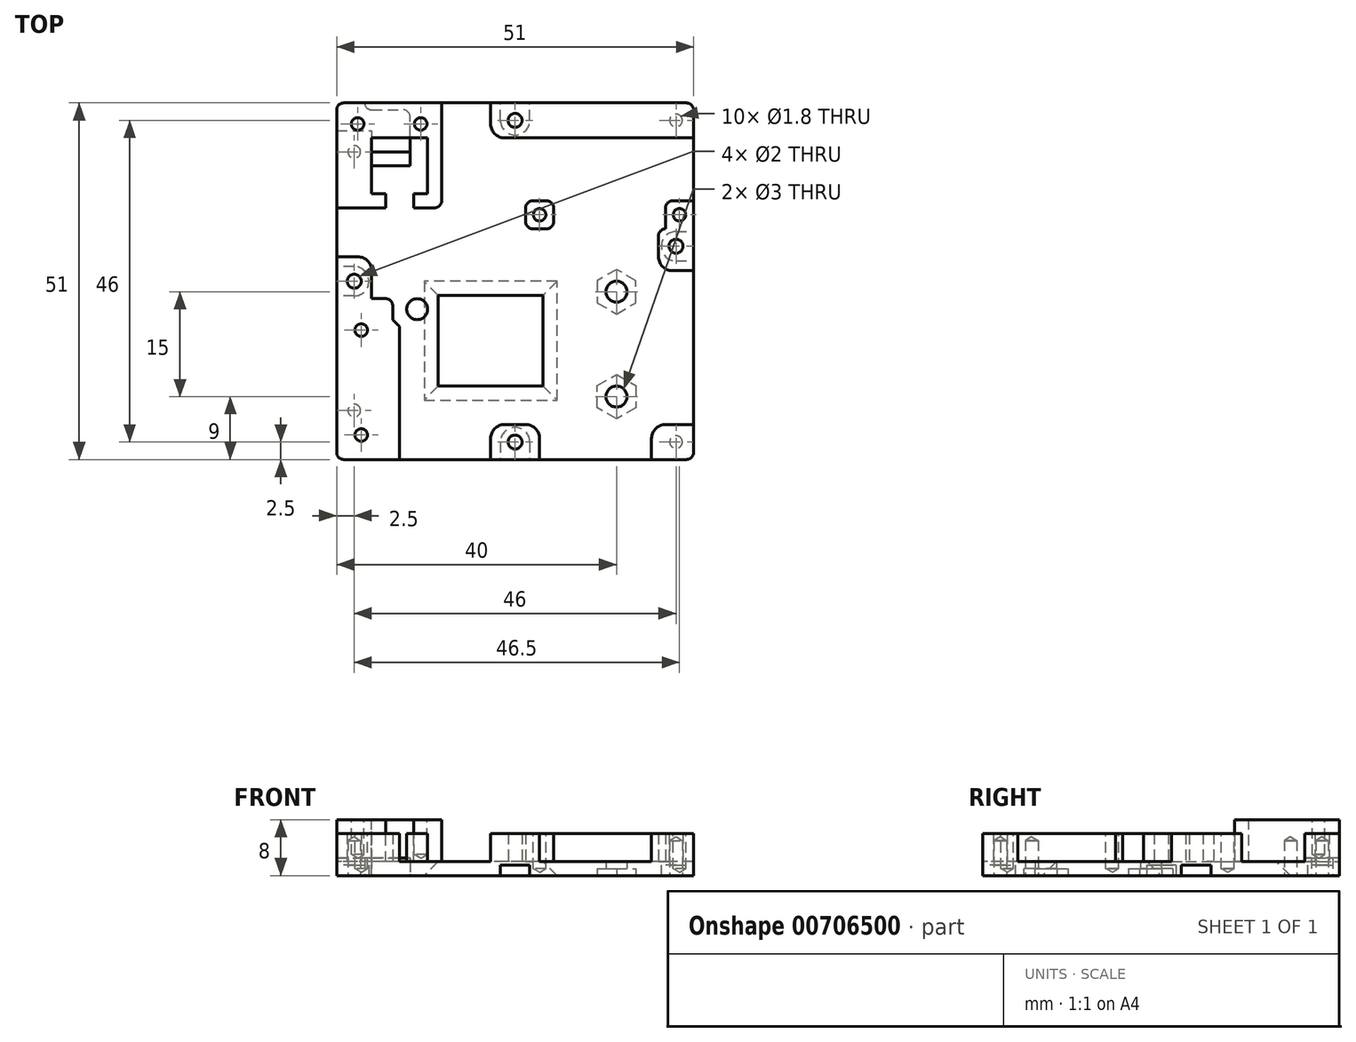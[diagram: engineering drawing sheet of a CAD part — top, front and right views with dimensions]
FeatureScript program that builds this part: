
annotation { "Feature Type Name" : "Feature", "Feature Type Description" : "" }
export const myFeature = defineFeature(function(context is Context, id is Id, definition is map)
    precondition{}
    {
        {
            var Q0;
            Q0=qCreatedBy(makeId("Top.planeOp"),FACE);
            var sketch = newSketch(context, id + "F0", { "sketchPlane" : qUnion([Q0])});
            skLineSegment(sketch, "E0.bottom", {"start": v(24.5, -25.5) * mm, "end": v(-24.5, -25.5) * mm});
            skLineSegment(sketch, "E0.top", {"start": v(24.5, 25.5) * mm, "end": v(-24.5, 25.5) * mm});
            skLineSegment(sketch, "E0.left", {"start": v(25.5, -24.5) * mm, "end": v(25.5, 24.5) * mm});
            skLineSegment(sketch, "E0.right", {"start": v(-25.5, -24.5) * mm, "end": v(-25.5, 24.5) * mm});
            skPoint(sketch, "E0.middle", {"position": v(0, 0) * mm});
            skPoint(sketch, "E1.visualSharp", {"position": v(-25.5, 25.5) * mm});
            skArc(sketch, "E1.filletArc", {"start": v(-24.5, 25.5) * mm, "mid": v(-25.2, 25.2) * mm, "end": v(-25.5, 24.5) * mm});
            skPoint(sketch, "E2.visualSharp", {"position": v(25.5, 25.5) * mm});
            skArc(sketch, "E2.filletArc", {"start": v(25.5, 24.5) * mm, "mid": v(25.2, 25.2) * mm, "end": v(24.5, 25.5) * mm});
            skPoint(sketch, "E3.visualSharp", {"position": v(25.5, -25.5) * mm});
            skArc(sketch, "E3.filletArc", {"start": v(24.5, -25.5) * mm, "mid": v(25.2, -25.2) * mm, "end": v(25.5, -24.5) * mm});
            skPoint(sketch, "E4.visualSharp", {"position": v(-25.5, -25.5) * mm});
            skArc(sketch, "E4.filletArc", {"start": v(-25.5, -24.5) * mm, "mid": v(-25.2, -25.2) * mm, "end": v(-24.5, -25.5) * mm});
            skSolve(sketch);
        }
        {
            var Q0;
            Q0=makeQuery(id+"F0.imprint","IMPRINT",FACE,{"disambiguationData":[TD([[makeQuery(id+"F0.imprint","IMPRINT",EDGE,{"derivedFrom":sQuery(id+"F0.wireOp",EDGE,"E0.bottom")}),-1.0]])]});
            extrude(context, id + "F1", {"entities" : qUnion([Q0]), "depth" : 2 * mm, "offsetDistance" : 25 * mm});
        }
        {
            var Q0;
            Q0=makeQuery(id+"F1.opExtrude","CAP_FACE",FACE,{"disambiguationData":[OSD([sQuery(id+"F0.wireOp",EDGE,"E0.bottom"),sQuery(id+"F0.wireOp",EDGE,"E0.top"),sQuery(id+"F0.wireOp",EDGE,"E0.left"),sQuery(id+"F0.wireOp",EDGE,"E0.right"),sQuery(id+"F0.wireOp",EDGE,"E1.filletArc"),sQuery(id+"F0.wireOp",EDGE,"E2.filletArc"),sQuery(id+"F0.wireOp",EDGE,"E3.filletArc"),sQuery(id+"F0.wireOp",EDGE,"E4.filletArc")])],"isStart":false});
            var sketch = newSketch(context, id + "F2", { "sketchPlane" : qUnion([Q0])});
            skLineSegment(sketch, "E5.bottom", {"start": v(-20.5, -2.5) * mm, "end": v(-25.5, -2.5) * mm});
            skLineSegment(sketch, "E5.top", {"start": v(-20.5, 2.5) * mm, "end": v(-25.5, 2.5) * mm});
            skLineSegment(sketch, "E5.left", {"start": v(-20.5, -2.5) * mm, "end": v(-20.5, 2.5) * mm});
            skLineSegment(sketch, "E5.right", {"start": v(-25.5, -2.5) * mm, "end": v(-25.5, 2.5) * mm});
            skPoint(sketch, "E5.middle", {"position": v(-23, 0) * mm});
            skLineSegment(sketch, "E6.bottom", {"start": v(2.5, 20.5) * mm, "end": v(-2.5, 20.5) * mm});
            skLineSegment(sketch, "E6.top", {"start": v(2.5, 25.5) * mm, "end": v(-2.5, 25.5) * mm});
            skLineSegment(sketch, "E6.left", {"start": v(2.5, 20.5) * mm, "end": v(2.5, 25.5) * mm});
            skLineSegment(sketch, "E6.right", {"start": v(-2.5, 20.5) * mm, "end": v(-2.5, 25.5) * mm});
            skPoint(sketch, "E6.middle", {"position": v(0, 23) * mm});
            skLineSegment(sketch, "E7.MirrorCS", {"start": v(-2.5, -20.5) * mm, "end": v(-2.5, -25.5) * mm});
            skLineSegment(sketch, "E8.MirrorCS", {"start": v(2.5, -20.5) * mm, "end": v(-2.5, -20.5) * mm});
            skLineSegment(sketch, "E9.MirrorCS", {"start": v(2.5, -25.5) * mm, "end": v(-2.5, -25.5) * mm});
            skLineSegment(sketch, "E10.MirrorCS", {"start": v(2.5, -20.5) * mm, "end": v(2.5, -25.5) * mm});
            skPoint(sketch, "E11.MirrorP", {"position": v(0, -23) * mm});
            skLineSegment(sketch, "E12.bottom", {"start": v(25.5, 2.5) * mm, "end": v(20.5, 2.5) * mm});
            skLineSegment(sketch, "E12.top", {"start": v(25.5, 7.5) * mm, "end": v(20.5, 7.5) * mm});
            skLineSegment(sketch, "E12.left", {"start": v(25.5, 2.5) * mm, "end": v(25.5, 7.5) * mm});
            skLineSegment(sketch, "E12.right", {"start": v(20.5, 2.5) * mm, "end": v(20.5, 7.5) * mm});
            skPoint(sketch, "E12.middle", {"position": v(23, 5) * mm});
            skLineSegment(sketch, "E13.bottom", {"start": v(-10.5, 10.5) * mm, "end": v(-25.5, 10.5) * mm});
            skLineSegment(sketch, "E13.top", {"start": v(-10.5, 25.5) * mm, "end": v(-24.5, 25.5) * mm});
            skLineSegment(sketch, "E13.left", {"start": v(-10.5, 10.5) * mm, "end": v(-10.5, 25.5) * mm});
            skLineSegment(sketch, "E13.right", {"start": v(-25.5, 10.5) * mm, "end": v(-25.5, 24.5) * mm});
            skPoint(sketch, "E13.middle", {"position": v(-18, 18) * mm});
            skPoint(sketch, "E14.visualSharp", {"position": v(-25.5, 25.5) * mm});
            skArc(sketch, "E14.filletArc", {"start": v(-24.5, 25.5) * mm, "mid": v(-25.2, 25.2) * mm, "end": v(-25.5, 24.5) * mm});
            skLineSegment(sketch, "E15.bottom", {"start": v(4, -15) * mm, "end": v(-11, -15) * mm});
            skLineSegment(sketch, "E15.top", {"start": v(4, -2) * mm, "end": v(-11, -2) * mm});
            skLineSegment(sketch, "E15.left", {"start": v(4, -15) * mm, "end": v(4, -2) * mm});
            skLineSegment(sketch, "E15.right", {"start": v(-11, -15) * mm, "end": v(-11, -2) * mm});
            skPoint(sketch, "E15.middle", {"position": v(-3.5, -8.5) * mm});
            skSolve(sketch);
        }
        {
            var Q0;
            Q0=makeQuery(id+"F2.imprint","IMPRINT",FACE,{"disambiguationData":[TD([[makeQuery(id+"F2.imprint","IMPRINT",EDGE,{"derivedFrom":sQuery(id+"F2.wireOp",EDGE,"E5.bottom")}),-1.0]])]});
            var Q1;
            Q1=makeQuery(id+"F2.imprint","IMPRINT",FACE,{"disambiguationData":[TD([[makeQuery(id+"F2.imprint","IMPRINT",EDGE,{"derivedFrom":sQuery(id+"F2.wireOp",EDGE,"E6.bottom")}),-1.0]])]});
            var Q2;
            Q2=makeQuery(id+"F2.imprint","IMPRINT",FACE,{"disambiguationData":[TD([[makeQuery(id+"F2.imprint","IMPRINT",EDGE,{"derivedFrom":sQuery(id+"F2.wireOp",EDGE,"E12.bottom")}),-1.0]])]});
            var Q3;
            Q3=makeQuery(id+"F2.imprint","IMPRINT",FACE,{"disambiguationData":[TD([[makeQuery(id+"F2.imprint","IMPRINT",EDGE,{"derivedFrom":sQuery(id+"F2.wireOp",EDGE,"E7.MirrorCS")}),1.0]])]});
            extrude(context, id + "F3", {"entities" : qUnion([Q0, Q1, Q2, Q3]), "operationType" : NewBodyOperationType.ADD, "depth" : 4 * mm, "offsetDistance" : 25 * mm});
        }
        {
            var Q0;
            Q0=makeQuery(id+"F2.imprint","IMPRINT",FACE,{"disambiguationData":[TD([[makeQuery(id+"F2.imprint","IMPRINT",EDGE,{"derivedFrom":sQuery(id+"F2.wireOp",EDGE,"E13.bottom")}),-1.0]])]});
            extrude(context, id + "F4", {"entities" : qUnion([Q0]), "operationType" : NewBodyOperationType.ADD, "depth" : 6 * mm, "offsetDistance" : 25 * mm});
        }
        {
            var Q0;
            Q0=makeQuery(id+"F4.opExtrude","SWEPT_EDGE",EDGE,{"disambiguationData":[OSD([sQuery(id+"F2.wireOp",EDGE,"E13.bottom"),sQuery(id+"F2.wireOp",EDGE,"E13.left")])]});
            fillet(context, id + "F5", {"entities" : qUnion([Q0]), "radius" : 1 * mm, "tangentPropagation" : true, "allowEdgeOverflow" : false});
        }
        {
            var Q0;
            Q0=makeQuery(id+"F1.opExtrude","CAP_FACE",FACE,{"disambiguationData":[OSD([sQuery(id+"F0.wireOp",EDGE,"E0.bottom"),sQuery(id+"F0.wireOp",EDGE,"E0.top"),sQuery(id+"F0.wireOp",EDGE,"E0.left"),sQuery(id+"F0.wireOp",EDGE,"E0.right"),sQuery(id+"F0.wireOp",EDGE,"E1.filletArc"),sQuery(id+"F0.wireOp",EDGE,"E2.filletArc"),sQuery(id+"F0.wireOp",EDGE,"E3.filletArc"),sQuery(id+"F0.wireOp",EDGE,"E4.filletArc")])],"isStart":true});
            var sketch = newSketch(context, id + "F6", { "sketchPlane" : qUnion([Q0])});
            skPoint(sketch, "E16", {"position": v(0, 23) * mm});
            skPoint(sketch, "E17", {"position": v(-23, 0) * mm});
            skPoint(sketch, "E18", {"position": v(23, -5) * mm});
            skPoint(sketch, "E19.MirrorP", {"position": v(0, -23) * mm});
            skSolve(sketch);
        }
        {
            var Q0;
            Q0=sQuery(id+"F6.wireOp",VERTEX,"E17");
            var Q1;
            Q1=sQuery(id+"F6.wireOp",VERTEX,"E16");
            var Q2;
            Q2=sQuery(id+"F6.wireOp",VERTEX,"E18");
            var Q3;
            Q3=sQuery(id+"F6.wireOp",VERTEX,"E19.MirrorP");
            var Q4;
            Q4=makeQuery(id+"F1.opExtrude","SWEPT_BODY",BODY,{"disambiguationData":[OSD([sQuery(id+"F0.wireOp",EDGE,"E0.bottom"),sQuery(id+"F0.wireOp",EDGE,"E0.top"),sQuery(id+"F0.wireOp",EDGE,"E0.left"),sQuery(id+"F0.wireOp",EDGE,"E0.right"),sQuery(id+"F0.wireOp",EDGE,"E1.filletArc"),sQuery(id+"F0.wireOp",EDGE,"E2.filletArc"),sQuery(id+"F0.wireOp",EDGE,"E3.filletArc"),sQuery(id+"F0.wireOp",EDGE,"E4.filletArc")])]});
            hole(context, id + "F7", {"style" : HoleStyle.C_BORE, "endStyle" : HoleEndStyle.THROUGH, "holeDiameter" : 2 * mm, "cBoreDiameter" : 4.2 * mm, "cBoreDepth" : 1.5 * mm, "majorDiameter" : 5 * mm, "isTappedThrough" : true, "tappedDepth" : 6 * mm, "tapClearance" : 3, "locations" : qUnion([Q0, Q1, Q2, Q3]), "scope" : qUnion([Q4])});
        }
        {
            var Q0;
            Q0=makeQuery(id+"F2.imprint","IMPRINT",FACE,{"disambiguationData":[TD([[makeQuery(id+"F2.imprint","IMPRINT",EDGE,{"derivedFrom":sQuery(id+"F2.wireOp",EDGE,"E15.bottom")}),-1.0]])]});
            extrude(context, id + "F8", {"entities" : qUnion([Q0]), "operationType" : NewBodyOperationType.REMOVE, "oppositeDirection" : true, "depth" : 25 * mm, "offsetDistance" : 25 * mm});
        }
        {
            var Q0;
            Q0=makeQuery(id+"F8.boolean.opBoolean","INTERSECT",EDGE,{"derivedFrom":[makeQuery(id+"F1.opExtrude","CAP_FACE",FACE,{"disambiguationData":[OSD([sQuery(id+"F0.wireOp",EDGE,"E0.bottom"),sQuery(id+"F0.wireOp",EDGE,"E0.top"),sQuery(id+"F0.wireOp",EDGE,"E0.left"),sQuery(id+"F0.wireOp",EDGE,"E0.right"),sQuery(id+"F0.wireOp",EDGE,"E1.filletArc"),sQuery(id+"F0.wireOp",EDGE,"E2.filletArc"),sQuery(id+"F0.wireOp",EDGE,"E3.filletArc"),sQuery(id+"F0.wireOp",EDGE,"E4.filletArc")])],"isStart":true}),makeQuery(id+"F8.opExtrude","SWEPT_FACE",FACE,{"disambiguationData":[OSD([sQuery(id+"F2.wireOp",EDGE,"E15.right")])]})]});
            var Q1;
            Q1=makeQuery(id+"F8.boolean.opBoolean","INTERSECT",EDGE,{"derivedFrom":[makeQuery(id+"F1.opExtrude","CAP_FACE",FACE,{"disambiguationData":[OSD([sQuery(id+"F0.wireOp",EDGE,"E0.bottom"),sQuery(id+"F0.wireOp",EDGE,"E0.top"),sQuery(id+"F0.wireOp",EDGE,"E0.left"),sQuery(id+"F0.wireOp",EDGE,"E0.right"),sQuery(id+"F0.wireOp",EDGE,"E1.filletArc"),sQuery(id+"F0.wireOp",EDGE,"E2.filletArc"),sQuery(id+"F0.wireOp",EDGE,"E3.filletArc"),sQuery(id+"F0.wireOp",EDGE,"E4.filletArc")])],"isStart":true}),makeQuery(id+"F8.opExtrude","SWEPT_FACE",FACE,{"disambiguationData":[OSD([sQuery(id+"F2.wireOp",EDGE,"E15.bottom")])]})]});
            var Q2;
            Q2=makeQuery(id+"F8.boolean.opBoolean","INTERSECT",EDGE,{"derivedFrom":[makeQuery(id+"F1.opExtrude","CAP_FACE",FACE,{"disambiguationData":[OSD([sQuery(id+"F0.wireOp",EDGE,"E0.bottom"),sQuery(id+"F0.wireOp",EDGE,"E0.top"),sQuery(id+"F0.wireOp",EDGE,"E0.left"),sQuery(id+"F0.wireOp",EDGE,"E0.right"),sQuery(id+"F0.wireOp",EDGE,"E1.filletArc"),sQuery(id+"F0.wireOp",EDGE,"E2.filletArc"),sQuery(id+"F0.wireOp",EDGE,"E3.filletArc"),sQuery(id+"F0.wireOp",EDGE,"E4.filletArc")])],"isStart":true}),makeQuery(id+"F8.opExtrude","SWEPT_FACE",FACE,{"disambiguationData":[OSD([sQuery(id+"F2.wireOp",EDGE,"E15.left")])]})]});
            var Q3;
            Q3=makeQuery(id+"F8.boolean.opBoolean","INTERSECT",EDGE,{"derivedFrom":[makeQuery(id+"F1.opExtrude","CAP_FACE",FACE,{"disambiguationData":[OSD([sQuery(id+"F0.wireOp",EDGE,"E0.bottom"),sQuery(id+"F0.wireOp",EDGE,"E0.top"),sQuery(id+"F0.wireOp",EDGE,"E0.left"),sQuery(id+"F0.wireOp",EDGE,"E0.right"),sQuery(id+"F0.wireOp",EDGE,"E1.filletArc"),sQuery(id+"F0.wireOp",EDGE,"E2.filletArc"),sQuery(id+"F0.wireOp",EDGE,"E3.filletArc"),sQuery(id+"F0.wireOp",EDGE,"E4.filletArc")])],"isStart":true}),makeQuery(id+"F8.opExtrude","SWEPT_FACE",FACE,{"disambiguationData":[OSD([sQuery(id+"F2.wireOp",EDGE,"E15.top")])]})]});
            chamfer(context, id + "F9", {"entities" : qUnion([Q0, Q1, Q2, Q3]), "width" : 2 * mm, "tangentPropagation" : true});
        }
        {
            var Q0;
            {var subQ11=sQuery(id+"F2.wireOp",EDGE,"E5.bottom");Q0=makeQuery(id+"F2.imprint","IMPRINT",FACE,{"disambiguationData":[TD([[makeQuery(id+"F2.imprint","IMPRINT",EDGE,{"derivedFrom":subQ11}),1.0]])]});}
            var sketch = newSketch(context, id + "F10", { "sketchPlane" : qUnion([Q0])});
            skLineSegment(sketch, "E20.bottom", {"start": v(-16.5, -25.5) * mm, "end": v(-24.5, -25.5) * mm});
            skLineSegment(sketch, "E20.left", {"start": v(-12.5, -25.5) * mm, "end": v(-12.5, -4) * mm, "construction": true});
            skLineSegment(sketch, "E20.right", {"start": v(-25.5, -24.5) * mm, "end": v(-25.5, -2.5) * mm});
            skPoint(sketch, "E20.middle", {"position": v(-19, -14) * mm});
            skPoint(sketch, "E21.visualSharp", {"position": v(-25.5, -25.5) * mm});
            skArc(sketch, "E21.filletArc", {"start": v(-25.5, -24.5) * mm, "mid": v(-25.2, -25.2) * mm, "end": v(-24.5, -25.5) * mm});
            skCircle(sketch, "E22", {"center": v(-14, -4) * mm, "radius": 1.5 * mm});
            skLineSegment(sketch, "E23", {"start": v(-16.5, -6.5) * mm, "end": v(-16.5, -25.5) * mm});
            skLineSegment(sketch, "E24.trimOffspring", {"start": v(-18.5, -2.5) * mm, "end": v(-25.5, -2.5) * mm});
            skLineSegment(sketch, "E25", {"start": v(-17.5, -3.5) * mm, "end": v(-17.5, -5.5) * mm});
            skLineSegment(sketch, "E26", {"start": v(-16.5, -6.5) * mm, "end": v(-17.5, -5.5) * mm});
            skPoint(sketch, "E27.visualSharp", {"position": v(-17.5, -2.5) * mm});
            skArc(sketch, "E27.filletArc", {"start": v(-17.5, -3.5) * mm, "mid": v(-17.8, -2.8) * mm, "end": v(-18.5, -2.5) * mm});
            skSolve(sketch);
        }
        {
            var Q0;
            Q0=makeQuery(id+"F10.imprint","IMPRINT",FACE,{"disambiguationData":[TD([[makeQuery(id+"F10.imprint","IMPRINT",EDGE,{"derivedFrom":sQuery(id+"F10.wireOp",EDGE,"E20.bottom")}),-1.0]])]});
            var Q1;
            Q1=makeQuery(id+"F10.imprint","IMPRINT",FACE,{"disambiguationData":[TD([[makeQuery(id+"F10.imprint","IMPRINT",EDGE,{"derivedFrom":sQuery(id+"F10.wireOp",EDGE,"E22")}),1.0]])]});
            extrude(context, id + "F11", {"entities" : qUnion([Q0, Q1]), "operationType" : NewBodyOperationType.ADD, "depth" : 4 * mm, "offsetDistance" : 25 * mm});
        }
        {
            var Q0;
            Q0=makeQuery(id+"F11.boolean.opBoolean","MERGE",FACE,{"derivedFrom":[makeQuery(id+"F3.opExtrude","CAP_FACE",FACE,{"disambiguationData":[OSD([sQuery(id+"F2.wireOp",EDGE,"E5.bottom"),sQuery(id+"F2.wireOp",EDGE,"E5.top"),sQuery(id+"F2.wireOp",EDGE,"E5.left"),sQuery(id+"F2.wireOp",EDGE,"E5.right")])],"isStart":false}),makeQuery(id+"F11.opExtrude","CAP_FACE",FACE,{"disambiguationData":[OSD([sQuery(id+"F10.wireOp",EDGE,"E20.bottom"),sQuery(id+"F10.wireOp",EDGE,"E20.right"),sQuery(id+"F10.wireOp",EDGE,"E21.filletArc"),sQuery(id+"F10.wireOp",EDGE,"E23"),sQuery(id+"F10.wireOp",EDGE,"E24.trimOffspring"),sQuery(id+"F10.wireOp",EDGE,"E25"),sQuery(id+"F10.wireOp",EDGE,"E26"),sQuery(id+"F10.wireOp",EDGE,"E27.filletArc")])],"isStart":false})]});
            var sketch = newSketch(context, id + "F12", { "sketchPlane" : qUnion([Q0])});
            skPoint(sketch, "E28", {"position": v(-22, -22) * mm});
            skPoint(sketch, "E29", {"position": v(-22, -7) * mm});
            skSolve(sketch);
        }
        {
            var Q0;
            Q0=makeQuery(id+"F4.opExtrude","CAP_FACE",FACE,{"disambiguationData":[OSD([sQuery(id+"F2.wireOp",EDGE,"E13.bottom"),sQuery(id+"F2.wireOp",EDGE,"E13.top"),sQuery(id+"F2.wireOp",EDGE,"E13.left"),sQuery(id+"F2.wireOp",EDGE,"E13.right"),sQuery(id+"F2.wireOp",EDGE,"E14.filletArc")])],"isStart":false});
            var sketch = newSketch(context, id + "F13", { "sketchPlane" : qUnion([Q0])});
            skPoint(sketch, "E30", {"position": v(-22.5, 22.5) * mm});
            skPoint(sketch, "E31", {"position": v(-13.5, 22.5) * mm});
            skLineSegment(sketch, "E32.bottom", {"start": v(-12.5, 12.5) * mm, "end": v(-14.5, 12.5) * mm});
            skLineSegment(sketch, "E32.top", {"start": v(-12.5, 20.5) * mm, "end": v(-23.5, 20.5) * mm});
            skLineSegment(sketch, "E32.left", {"start": v(-12.5, 12.5) * mm, "end": v(-12.5, 20.5) * mm});
            skLineSegment(sketch, "E32.right", {"start": v(-23.5, 12.5) * mm, "end": v(-23.5, 20.5) * mm});
            skPoint(sketch, "E32.middle", {"position": v(-18, 16.5) * mm});
            skLineSegment(sketch, "E33", {"start": v(-14.5, 10.5) * mm, "end": v(-18.5, 10.5) * mm});
            skLineSegment(sketch, "E34", {"start": v(-18.5, 10.5) * mm, "end": v(-18.5, 12.5) * mm});
            skLineSegment(sketch, "E35", {"start": v(-14.5, 10.5) * mm, "end": v(-14.5, 12.5) * mm});
            skLineSegment(sketch, "E36.trimOffspring", {"start": v(-18.5, 12.5) * mm, "end": v(-23.5, 12.5) * mm});
            skSolve(sketch);
        }
        {
            var Q0;
            Q0=makeQuery(id+"F13.imprint","IMPRINT",FACE,{"disambiguationData":[TD([[makeQuery(id+"F13.imprint","IMPRINT",EDGE,{"derivedFrom":sQuery(id+"F13.wireOp",EDGE,"E32.bottom")}),-1.0]])]});
            extrude(context, id + "F14", {"entities" : qUnion([Q0]), "operationType" : NewBodyOperationType.REMOVE, "oppositeDirection" : true, "depth" : 6 * mm, "offsetDistance" : 25 * mm});
        }
        {
            var Q0;
            Q0=makeQuery(id+"F1.opExtrude","CAP_FACE",FACE,{"disambiguationData":[OSD([sQuery(id+"F0.wireOp",EDGE,"E0.bottom"),sQuery(id+"F0.wireOp",EDGE,"E0.top"),sQuery(id+"F0.wireOp",EDGE,"E0.left"),sQuery(id+"F0.wireOp",EDGE,"E0.right"),sQuery(id+"F0.wireOp",EDGE,"E1.filletArc"),sQuery(id+"F0.wireOp",EDGE,"E2.filletArc"),sQuery(id+"F0.wireOp",EDGE,"E3.filletArc"),sQuery(id+"F0.wireOp",EDGE,"E4.filletArc")])],"isStart":true});
            var sketch = newSketch(context, id + "F15", { "sketchPlane" : qUnion([Q0])});
            skCircle(sketch, "E37.0", {"center": v(0, 23) * mm, "radius": 2.1 * mm});
            skCircle(sketch, "E37.1", {"center": v(-23, 0) * mm, "radius": 2.1 * mm});
            skCircle(sketch, "E37.2", {"center": v(0, -23) * mm, "radius": 2.1 * mm});
            skCircle(sketch, "E37.3", {"center": v(23, -5) * mm, "radius": 2.1 * mm});
            skLineSegment(sketch, "E38", {"start": v(2.1, 23) * mm, "end": v(2.1, 25.5) * mm});
            skLineSegment(sketch, "E39.MirrorCS", {"start": v(-2.1, 23) * mm, "end": v(-2.1, 25.5) * mm});
            skLineSegment(sketch, "E40.MirrorCS", {"start": v(-2.1, -23) * mm, "end": v(-2.1, -25.5) * mm});
            skLineSegment(sketch, "E41.MirrorCS", {"start": v(2.1, -23) * mm, "end": v(2.1, -25.5) * mm});
            skLineSegment(sketch, "E42", {"start": v(-23, 2.1) * mm, "end": v(-25.5, 2.1) * mm});
            skLineSegment(sketch, "E43.MirrorCS", {"start": v(-23, -2.1) * mm, "end": v(-25.5, -2.1) * mm});
            skLineSegment(sketch, "E44", {"start": v(23, -2.9) * mm, "end": v(25.5, -2.9) * mm});
            skLineSegment(sketch, "E45", {"start": v(23, -7.1) * mm, "end": v(25.5, -7.1) * mm});
            skSolve(sketch);
        }
        {
            var Q0;
            {var subQ0=sQuery(id+"F15.wireOp",EDGE,"E38");Q0=makeQuery(id+"F15.imprint","IMPRINT",FACE,{"disambiguationData":[TD([[makeQuery(id+"F15.imprint","IMPRINT",EDGE,{"derivedFrom":subQ0}),1.0]])]});}
            var Q1;
            {var subQ0=sQuery(id+"F15.wireOp",EDGE,"E44");Q1=makeQuery(id+"F15.imprint","IMPRINT",FACE,{"disambiguationData":[TD([[makeQuery(id+"F15.imprint","IMPRINT",EDGE,{"derivedFrom":subQ0}),-1.0]])]});}
            var Q2;
            {var subQ0=sQuery(id+"F15.wireOp",EDGE,"E42");Q2=makeQuery(id+"F15.imprint","IMPRINT",FACE,{"disambiguationData":[TD([[makeQuery(id+"F15.imprint","IMPRINT",EDGE,{"derivedFrom":subQ0}),1.0]])]});}
            var Q3;
            {var subQ0=sQuery(id+"F15.wireOp",EDGE,"E40.MirrorCS");Q3=makeQuery(id+"F15.imprint","IMPRINT",FACE,{"disambiguationData":[TD([[makeQuery(id+"F15.imprint","IMPRINT",EDGE,{"derivedFrom":subQ0}),1.0]])]});}
            extrude(context, id + "F16", {"entities" : qUnion([Q0, Q1, Q2, Q3]), "operationType" : NewBodyOperationType.REMOVE, "oppositeDirection" : true, "depth" : 1.5 * mm, "offsetDistance" : 25 * mm});
        }
        {
            var Q0;
            Q0=makeQuery(id+"F1.opExtrude","CAP_FACE",FACE,{"disambiguationData":[OSD([sQuery(id+"F0.wireOp",EDGE,"E0.bottom"),sQuery(id+"F0.wireOp",EDGE,"E0.top"),sQuery(id+"F0.wireOp",EDGE,"E0.left"),sQuery(id+"F0.wireOp",EDGE,"E0.right"),sQuery(id+"F0.wireOp",EDGE,"E1.filletArc"),sQuery(id+"F0.wireOp",EDGE,"E2.filletArc"),sQuery(id+"F0.wireOp",EDGE,"E3.filletArc"),sQuery(id+"F0.wireOp",EDGE,"E4.filletArc")])],"isStart":true});
            var sketch = newSketch(context, id + "F17", { "sketchPlane" : qUnion([Q0])});
            skPoint(sketch, "E46", {"position": v(14.5, 1.5) * mm});
            skPoint(sketch, "E47", {"position": v(14.5, 16.5) * mm});
            skCircle(sketch, "E48.cCircle", {"center": v(14.5, 1.5) * mm, "radius": 2.75 * mm, "construction": true});
            skLineSegment(sketch, "E48.0", {"start": v(17.25, 3.09) * mm, "end": v(17.25, -0.09) * mm});
            skLineSegment(sketch, "E48.1", {"start": v(17.25, -0.09) * mm, "end": v(14.5, -1.68) * mm});
            skLineSegment(sketch, "E48.2", {"start": v(14.5, -1.68) * mm, "end": v(11.75, -0.09) * mm});
            skLineSegment(sketch, "E48.3", {"start": v(11.75, -0.09) * mm, "end": v(11.75, 3.09) * mm});
            skLineSegment(sketch, "E48.4", {"start": v(11.75, 3.09) * mm, "end": v(14.5, 4.68) * mm});
            skLineSegment(sketch, "E48.5", {"start": v(14.5, 4.68) * mm, "end": v(17.25, 3.09) * mm});
            skPoint(sketch, "E48.0.midPoint", {"position": v(17.25, 1.5) * mm});
            skLineSegment(sketch, "E49", {"start": v(42.06, 9) * mm, "end": v(-2.43, 9) * mm, "construction": true});
            skCircle(sketch, "E50.MirrorC", {"center": v(14.5, 16.5) * mm, "radius": 2.75 * mm, "construction": true});
            skLineSegment(sketch, "E51.MirrorCS", {"start": v(14.5, 19.68) * mm, "end": v(11.75, 18.09) * mm});
            skLineSegment(sketch, "E52.MirrorCS", {"start": v(17.25, 18.09) * mm, "end": v(14.5, 19.68) * mm});
            skLineSegment(sketch, "E53.MirrorCS", {"start": v(17.25, 14.91) * mm, "end": v(17.25, 18.09) * mm});
            skLineSegment(sketch, "E54.MirrorCS", {"start": v(14.5, 13.32) * mm, "end": v(17.25, 14.91) * mm});
            skLineSegment(sketch, "E55.MirrorCS", {"start": v(11.75, 14.91) * mm, "end": v(14.5, 13.32) * mm});
            skLineSegment(sketch, "E56.MirrorCS", {"start": v(11.75, 18.09) * mm, "end": v(11.75, 14.91) * mm});
            skSolve(sketch);
        }
        {
            var Q0;
            Q0=makeQuery(id+"F17.imprint","IMPRINT",FACE,{"disambiguationData":[TD([[makeQuery(id+"F17.imprint","IMPRINT",EDGE,{"derivedFrom":sQuery(id+"F17.wireOp",EDGE,"E51.MirrorCS")}),1.0]])]});
            var Q1;
            Q1=makeQuery(id+"F17.imprint","IMPRINT",FACE,{"disambiguationData":[TD([[makeQuery(id+"F17.imprint","IMPRINT",EDGE,{"derivedFrom":sQuery(id+"F17.wireOp",EDGE,"E48.0")}),-1.0]])]});
            extrude(context, id + "F18", {"entities" : qUnion([Q0, Q1]), "operationType" : NewBodyOperationType.REMOVE, "oppositeDirection" : true, "depth" : 1 * mm, "offsetDistance" : 25 * mm});
        }
        {
            var Q0;
            Q0=sQuery(id+"F17.wireOp",VERTEX,"E50.MirrorC.center");
            var Q1;
            Q1=sQuery(id+"F17.wireOp",VERTEX,"E46");
            var Q2;
            Q2=makeQuery(id+"F1.opExtrude","SWEPT_BODY",BODY,{"disambiguationData":[OSD([sQuery(id+"F0.wireOp",EDGE,"E0.bottom"),sQuery(id+"F0.wireOp",EDGE,"E0.top"),sQuery(id+"F0.wireOp",EDGE,"E0.left"),sQuery(id+"F0.wireOp",EDGE,"E0.right"),sQuery(id+"F0.wireOp",EDGE,"E1.filletArc"),sQuery(id+"F0.wireOp",EDGE,"E2.filletArc"),sQuery(id+"F0.wireOp",EDGE,"E3.filletArc"),sQuery(id+"F0.wireOp",EDGE,"E4.filletArc")])]});
            hole(context, id + "F19", {"style" : HoleStyle.SIMPLE, "endStyle" : HoleEndStyle.THROUGH, "holeDiameter" : 3 * mm, "majorDiameter" : 5 * mm, "isTappedThrough" : true, "tappedDepth" : 6 * mm, "tapClearance" : 3, "locations" : qUnion([Q0, Q1]), "scope" : qUnion([Q2])});
        }
        {
            var Q0;
            Q0=makeQuery(id+"F14.boolean.opBoolean","MERGE",FACE,{"derivedFrom":[makeQuery(id+"F1.opExtrude","CAP_FACE",FACE,{"disambiguationData":[OSD([sQuery(id+"F0.wireOp",EDGE,"E0.bottom"),sQuery(id+"F0.wireOp",EDGE,"E0.top"),sQuery(id+"F0.wireOp",EDGE,"E0.left"),sQuery(id+"F0.wireOp",EDGE,"E0.right"),sQuery(id+"F0.wireOp",EDGE,"E1.filletArc"),sQuery(id+"F0.wireOp",EDGE,"E2.filletArc"),sQuery(id+"F0.wireOp",EDGE,"E3.filletArc"),sQuery(id+"F0.wireOp",EDGE,"E4.filletArc")])],"isStart":false}),makeQuery(id+"F14.opExtrude","CAP_FACE",FACE,{"disambiguationData":[OSD([sQuery(id+"F13.wireOp",EDGE,"E32.bottom"),sQuery(id+"F13.wireOp",EDGE,"E32.top"),sQuery(id+"F13.wireOp",EDGE,"E32.left"),sQuery(id+"F13.wireOp",EDGE,"E32.right"),sQuery(id+"F13.wireOp",EDGE,"E33"),sQuery(id+"F13.wireOp",EDGE,"E34"),sQuery(id+"F13.wireOp",EDGE,"E35"),sQuery(id+"F13.wireOp",EDGE,"E36.trimOffspring")])],"isStart":false})]});
            var sketch = newSketch(context, id + "F20", { "sketchPlane" : qUnion([Q0])});
            skLineSegment(sketch, "E57.bottom", {"start": v(25.5, 7.5) * mm, "end": v(21.5, 7.5) * mm});
            skLineSegment(sketch, "E57.top", {"start": v(25.5, 11.5) * mm, "end": v(21.5, 11.5) * mm});
            skLineSegment(sketch, "E57.left", {"start": v(25.5, 7.5) * mm, "end": v(25.5, 11.5) * mm});
            skLineSegment(sketch, "E57.right", {"start": v(21.5, 7.5) * mm, "end": v(21.5, 11.5) * mm});
            skLineSegment(sketch, "E58.bottom", {"start": v(5.5, 7.5) * mm, "end": v(1.5, 7.5) * mm});
            skLineSegment(sketch, "E58.top", {"start": v(5.5, 11.5) * mm, "end": v(1.5, 11.5) * mm});
            skLineSegment(sketch, "E58.left", {"start": v(5.5, 7.5) * mm, "end": v(5.5, 11.5) * mm});
            skLineSegment(sketch, "E58.right", {"start": v(1.5, 7.5) * mm, "end": v(1.5, 11.5) * mm});
            skLineSegment(sketch, "E59.bottom", {"start": v(2.5, 25.5) * mm, "end": v(25.5, 25.5) * mm});
            skLineSegment(sketch, "E59.top", {"start": v(2.5, 20.5) * mm, "end": v(25.5, 20.5) * mm});
            skLineSegment(sketch, "E59.left", {"start": v(2.5, 25.5) * mm, "end": v(2.5, 20.5) * mm});
            skLineSegment(sketch, "E59.right", {"start": v(25.5, 25.5) * mm, "end": v(25.5, 20.5) * mm});
            skLineSegment(sketch, "E60.bottom", {"start": v(25.5, -25.5) * mm, "end": v(20.5, -25.5) * mm});
            skLineSegment(sketch, "E60.top", {"start": v(25.5, -20.5) * mm, "end": v(20.5, -20.5) * mm});
            skLineSegment(sketch, "E60.left", {"start": v(25.5, -25.5) * mm, "end": v(25.5, -20.5) * mm});
            skLineSegment(sketch, "E60.right", {"start": v(20.5, -25.5) * mm, "end": v(20.5, -20.5) * mm});
            skPoint(sketch, "E60.middle", {"position": v(23, -23) * mm});
            skSolve(sketch);
        }
        {
            var Q0;
            Q0=makeQuery(id+"F20.imprint","IMPRINT",FACE,{"disambiguationData":[TD([[makeQuery(id+"F20.imprint","IMPRINT",EDGE,{"derivedFrom":sQuery(id+"F20.wireOp",EDGE,"E57.bottom")}),-1.0]])]});
            var Q1;
            Q1=makeQuery(id+"F20.imprint","IMPRINT",FACE,{"disambiguationData":[TD([[makeQuery(id+"F20.imprint","IMPRINT",EDGE,{"derivedFrom":sQuery(id+"F20.wireOp",EDGE,"E58.bottom")}),-1.0]])]});
            var Q2;
            {var subQ1=sQuery(id+"F20.wireOp",EDGE,"E59.top");Q2=makeQuery(id+"F20.imprint","IMPRINT",FACE,{"disambiguationData":[TD([[makeQuery(id+"F20.imprint","IMPRINT",EDGE,{"derivedFrom":subQ1}),1.0]])]});}
            var Q3;
            {var subQ3=sQuery(id+"F20.wireOp",EDGE,"E60.top");Q3=makeQuery(id+"F20.imprint","IMPRINT",FACE,{"disambiguationData":[TD([[makeQuery(id+"F20.imprint","IMPRINT",EDGE,{"derivedFrom":subQ3}),1.0]])]});}
            extrude(context, id + "F21", {"entities" : qUnion([Q0, Q1, Q2, Q3]), "operationType" : NewBodyOperationType.ADD, "depth" : 4 * mm, "offsetDistance" : 25 * mm});
        }
        {
            var Q0;
            Q0=makeQuery(id+"F21.opExtrude","SWEPT_EDGE",EDGE,{"disambiguationData":[OSD([sQuery(id+"F20.wireOp",EDGE,"E58.bottom"),sQuery(id+"F20.wireOp",EDGE,"E58.left")])]});
            var Q1;
            Q1=makeQuery(id+"F21.opExtrude","SWEPT_EDGE",EDGE,{"disambiguationData":[OSD([sQuery(id+"F20.wireOp",EDGE,"E58.bottom"),sQuery(id+"F20.wireOp",EDGE,"E58.right")])]});
            var Q2;
            Q2=makeQuery(id+"F21.opExtrude","SWEPT_EDGE",EDGE,{"disambiguationData":[OSD([sQuery(id+"F20.wireOp",EDGE,"E58.top"),sQuery(id+"F20.wireOp",EDGE,"E58.right")])]});
            var Q3;
            Q3=makeQuery(id+"F3.opExtrude","SWEPT_EDGE",EDGE,{"disambiguationData":[OSD([sQuery(id+"F2.wireOp",EDGE,"E12.top"),sQuery(id+"F2.wireOp",EDGE,"E12.right")])]});
            var Q4;
            Q4=makeQuery(id+"F21.opExtrude","SWEPT_EDGE",EDGE,{"disambiguationData":[OSD([sQuery(id+"F20.wireOp",EDGE,"E58.top"),sQuery(id+"F20.wireOp",EDGE,"E58.left")])]});
            var Q5;
            Q5=makeQuery(id+"F21.opExtrude","SWEPT_EDGE",EDGE,{"disambiguationData":[OSD([sQuery(id+"F20.wireOp",EDGE,"E57.top"),sQuery(id+"F20.wireOp",EDGE,"E57.right")])]});
            fillet(context, id + "F22", {"entities" : qUnion([Q0, Q1, Q2, Q3, Q4, Q5]), "radius" : 1 * mm, "tangentPropagation" : true, "allowEdgeOverflow" : false});
        }
        {
            var Q0;
            Q0=makeQuery(id+"F21.opExtrude","CAP_FACE",FACE,{"disambiguationData":[OSD([sQuery(id+"F20.wireOp",EDGE,"E58.bottom"),sQuery(id+"F20.wireOp",EDGE,"E58.top"),sQuery(id+"F20.wireOp",EDGE,"E58.left"),sQuery(id+"F20.wireOp",EDGE,"E58.right")])],"isStart":false});
            var sketch = newSketch(context, id + "F23", { "sketchPlane" : qUnion([Q0])});
            skPoint(sketch, "E61", {"position": v(3.5, 9.5) * mm});
            skPoint(sketch, "E62", {"position": v(23.5, 9.5) * mm});
            skSolve(sketch);
        }
        {
            var Q0;
            Q0=sQuery(id+"F12.wireOp",VERTEX,"E28");
            var Q1;
            Q1=sQuery(id+"F12.wireOp",VERTEX,"E29");
            var Q2;
            Q2=sQuery(id+"F13.wireOp",VERTEX,"E30");
            var Q3;
            Q3=sQuery(id+"F13.wireOp",VERTEX,"E31");
            var Q4;
            Q4=sQuery(id+"F23.wireOp",VERTEX,"E61");
            var Q5;
            Q5=sQuery(id+"F23.wireOp",VERTEX,"E62");
            var Q6;
            Q6=makeQuery(id+"F1.opExtrude","SWEPT_BODY",BODY,{"disambiguationData":[OSD([sQuery(id+"F0.wireOp",EDGE,"E0.bottom"),sQuery(id+"F0.wireOp",EDGE,"E0.top"),sQuery(id+"F0.wireOp",EDGE,"E0.left"),sQuery(id+"F0.wireOp",EDGE,"E0.right"),sQuery(id+"F0.wireOp",EDGE,"E1.filletArc"),sQuery(id+"F0.wireOp",EDGE,"E2.filletArc"),sQuery(id+"F0.wireOp",EDGE,"E3.filletArc"),sQuery(id+"F0.wireOp",EDGE,"E4.filletArc")])]});
            hole(context, id + "F24", {"style" : HoleStyle.SIMPLE, "endStyle" : HoleEndStyle.BLIND, "holeDiameter" : 1.8 * mm, "majorDiameter" : 5 * mm, "holeDepth" : 5 * mm, "isTappedThrough" : true, "tappedDepth" : 6 * mm, "tapClearance" : 3, "locations" : qUnion([Q0, Q1, Q2, Q3, Q4, Q5]), "scope" : qUnion([Q6])});
        }
        {
            var Q0;
            Q0=makeQuery(id+"F14.boolean.opBoolean","COPY",FACE,{"derivedFrom":makeQuery(id+"F14.opExtrude","SWEPT_FACE",FACE,{"disambiguationData":[OSD([sQuery(id+"F13.wireOp",EDGE,"E32.right")])]})});
            extrude(context, id + "F25", {"entities" : qUnion([Q0]), "operationType" : NewBodyOperationType.ADD, "depth" : 3 * mm, "offsetDistance" : 25 * mm});
        }
        {
            var Q0;
            Q0=makeQuery(id+"F1.opExtrude","CAP_FACE",FACE,{"disambiguationData":[OSD([sQuery(id+"F0.wireOp",EDGE,"E0.bottom"),sQuery(id+"F0.wireOp",EDGE,"E0.top"),sQuery(id+"F0.wireOp",EDGE,"E0.left"),sQuery(id+"F0.wireOp",EDGE,"E0.right"),sQuery(id+"F0.wireOp",EDGE,"E1.filletArc"),sQuery(id+"F0.wireOp",EDGE,"E2.filletArc"),sQuery(id+"F0.wireOp",EDGE,"E3.filletArc"),sQuery(id+"F0.wireOp",EDGE,"E4.filletArc")])],"isStart":true});
            var sketch = newSketch(context, id + "F26", { "sketchPlane" : qUnion([Q0])});
            skLineSegment(sketch, "E63.bottom", {"start": v(-21.5, -21.5) * mm, "end": v(-25.5, -21.5) * mm});
            skLineSegment(sketch, "E63.top", {"start": v(-21.5, -25.5) * mm, "end": v(-25.5, -25.5) * mm});
            skLineSegment(sketch, "E63.left", {"start": v(-21.5, -24.5) * mm, "end": v(-21.5, -25.5) * mm});
            skLineSegment(sketch, "E63.right", {"start": v(-25.5, -21.5) * mm, "end": v(-25.5, -25.5) * mm});
            skPoint(sketch, "E63.middle", {"position": v(-23.5, -23.5) * mm});
            skLineSegment(sketch, "E64.top", {"start": v(-21.5, -24.5) * mm, "end": v(-15, -24.5) * mm});
            skLineSegment(sketch, "E64.right", {"start": v(-15, -21) * mm, "end": v(-15, -24.5) * mm});
            skLineSegment(sketch, "E65.right", {"start": v(-15, -21) * mm, "end": v(-15, -18.5) * mm});
            skLineSegment(sketch, "E66", {"start": v(-21.5, -21.5) * mm, "end": v(-20.5, -21.5) * mm});
            skLineSegment(sketch, "E67", {"start": v(-20.5, -21.5) * mm, "end": v(-20.5, -18.5) * mm});
            skLineSegment(sketch, "E68", {"start": v(-20.5, -18.5) * mm, "end": v(-15, -18.5) * mm});
            skSolve(sketch);
        }
        {
            var Q0;
            Q0=makeQuery(id+"F26.imprint","IMPRINT",FACE,{"disambiguationData":[TD([[makeQuery(id+"F26.imprint","IMPRINT",EDGE,{"derivedFrom":sQuery(id+"F26.wireOp",EDGE,"E64.top")}),1.0]])]});
            var Q1;
            Q1=makeQuery(id+"F26.imprint","IMPRINT",FACE,{"disambiguationData":[TD([[makeQuery(id+"F26.imprint","IMPRINT",EDGE,{"derivedFrom":sQuery(id+"F26.wireOp",EDGE,"E65.bottom")}),1.0]])]});
            var Q2;
            {var subQ10=sQuery(id+"F26.wireOp",EDGE,"E63.bottom");Q2=makeQuery(id+"F26.imprint","IMPRINT",FACE,{"disambiguationData":[TD([[makeQuery(id+"F26.imprint","IMPRINT",EDGE,{"derivedFrom":subQ10}),1.0]])]});}
            extrude(context, id + "F27", {"entities" : qUnion([Q0, Q1, Q2]), "operationType" : NewBodyOperationType.REMOVE, "oppositeDirection" : true, "depth" : 2.5 * mm, "offsetDistance" : 25 * mm});
        }
        {
            var Q0;
            Q0=makeQuery(id+"F27.boolean.opBoolean","INTERSECT",EDGE,{"derivedFrom":[makeQuery(id+"F14.boolean.opBoolean","MERGE",FACE,{"derivedFrom":[makeQuery(id+"F1.opExtrude","CAP_FACE",FACE,{"disambiguationData":[OSD([sQuery(id+"F0.wireOp",EDGE,"E0.bottom"),sQuery(id+"F0.wireOp",EDGE,"E0.top"),sQuery(id+"F0.wireOp",EDGE,"E0.left"),sQuery(id+"F0.wireOp",EDGE,"E0.right"),sQuery(id+"F0.wireOp",EDGE,"E1.filletArc"),sQuery(id+"F0.wireOp",EDGE,"E2.filletArc"),sQuery(id+"F0.wireOp",EDGE,"E3.filletArc"),sQuery(id+"F0.wireOp",EDGE,"E4.filletArc")])],"isStart":false}),makeQuery(id+"F14.opExtrude","CAP_FACE",FACE,{"disambiguationData":[OSD([sQuery(id+"F13.wireOp",EDGE,"E32.bottom"),sQuery(id+"F13.wireOp",EDGE,"E32.top"),sQuery(id+"F13.wireOp",EDGE,"E32.left"),sQuery(id+"F13.wireOp",EDGE,"E32.right"),sQuery(id+"F13.wireOp",EDGE,"E33"),sQuery(id+"F13.wireOp",EDGE,"E34"),sQuery(id+"F13.wireOp",EDGE,"E35"),sQuery(id+"F13.wireOp",EDGE,"E36.trimOffspring")])],"isStart":false})]}),makeQuery(id+"F27.opExtrude","SWEPT_FACE",FACE,{"disambiguationData":[OSD([sQuery(id+"F26.wireOp",EDGE,"E68")])]})]});
            chamfer(context, id + "F28", {"entities" : qUnion([Q0]), "width" : 2 * mm, "tangentPropagation" : true});
        }
        {
            var Q0;
            Q0=makeQuery(id+"F27.boolean.opBoolean","COPY",EDGE,{"derivedFrom":makeQuery(id+"F27.opExtrude","SWEPT_EDGE",EDGE,{"disambiguationData":[OSD([sQuery(id+"F26.wireOp",EDGE,"E63.bottom"),sQuery(id+"F26.wireOp",EDGE,"E65.left")])]})});
            var Q1;
            Q1=makeQuery(id+"F27.boolean.opBoolean","COPY",EDGE,{"derivedFrom":makeQuery(id+"F27.opExtrude","SWEPT_EDGE",EDGE,{"disambiguationData":[OSD([sQuery(id+"F26.wireOp",EDGE,"E63.left"),sQuery(id+"F26.wireOp",EDGE,"E64.top")])]})});
            var Q2;
            Q2=makeQuery(id+"F27.boolean.opBoolean","COPY",EDGE,{"derivedFrom":makeQuery(id+"F27.opExtrude","SWEPT_EDGE",EDGE,{"disambiguationData":[OSD([sQuery(id+"F26.wireOp",EDGE,"E64.top"),sQuery(id+"F26.wireOp",EDGE,"E64.right")])]})});
            fillet(context, id + "F29", {"entities" : qUnion([Q0, Q1, Q2]), "radius" : 1 * mm, "tangentPropagation" : true, "allowEdgeOverflow" : false});
        }
        {
            var Q0;
            Q0=makeQuery(id+"F3.opExtrude","SWEPT_FACE",FACE,{"disambiguationData":[OSD([sQuery(id+"F2.wireOp",EDGE,"E6.right")])]});
            var Q1;
            Q1=makeQuery(id+"F3.opExtrude","SWEPT_FACE",FACE,{"disambiguationData":[OSD([sQuery(id+"F2.wireOp",EDGE,"E7.MirrorCS")])]});
            var Q2;
            Q2=makeQuery(id+"F21.opExtrude","SWEPT_FACE",FACE,{"disambiguationData":[OSD([sQuery(id+"F20.wireOp",EDGE,"E60.right")])]});
            extrude(context, id + "F30", {"entities" : qUnion([Q0, Q1, Q2]), "operationType" : NewBodyOperationType.ADD, "depth" : 1 * mm, "offsetDistance" : 25 * mm});
        }
        {
            var Q0;
            Q0=makeQuery(id+"F3.opExtrude","SWEPT_FACE",FACE,{"disambiguationData":[OSD([sQuery(id+"F2.wireOp",EDGE,"E10.MirrorCS")])]});
            extrude(context, id + "F31", {"entities" : qUnion([Q0]), "operationType" : NewBodyOperationType.ADD, "depth" : 1 * mm, "offsetDistance" : 25 * mm});
        }
        {
            var Q0;
            Q0=makeQuery(id+"F3.opExtrude","SWEPT_FACE",FACE,{"disambiguationData":[OSD([sQuery(id+"F2.wireOp",EDGE,"E12.bottom")])]});
            extrude(context, id + "F32", {"entities" : qUnion([Q0]), "operationType" : NewBodyOperationType.ADD, "depth" : 1 * mm, "offsetDistance" : 25 * mm});
        }
        {
            var Q0;
            Q0=makeQuery(id+"F3.opExtrude","SWEPT_FACE",FACE,{"disambiguationData":[OSD([sQuery(id+"F2.wireOp",EDGE,"E5.top")])]});
            extrude(context, id + "F33", {"entities" : qUnion([Q0]), "operationType" : NewBodyOperationType.ADD, "depth" : 1 * mm, "offsetDistance" : 25 * mm});
        }
        {
            var Q0;
            Q0=makeQuery(id+"F30.opExtrude","CAP_EDGE",EDGE,{"disambiguationData":[OSD([sQuery(id+"F20.wireOp",EDGE,"E60.top"),sQuery(id+"F20.wireOp",EDGE,"E60.right")])],"isStart":false});
            var Q1;
            Q1=makeQuery(id+"F32.opExtrude","CAP_EDGE",EDGE,{"disambiguationData":[OSD([sQuery(id+"F2.wireOp",EDGE,"E12.bottom"),sQuery(id+"F2.wireOp",EDGE,"E12.right")])],"isStart":false});
            var Q2;
            Q2=makeQuery(id+"F31.opExtrude","CAP_EDGE",EDGE,{"disambiguationData":[OSD([sQuery(id+"F2.wireOp",EDGE,"E8.MirrorCS"),sQuery(id+"F2.wireOp",EDGE,"E10.MirrorCS")])],"isStart":false});
            var Q3;
            Q3=makeQuery(id+"F30.opExtrude","CAP_EDGE",EDGE,{"disambiguationData":[OSD([sQuery(id+"F2.wireOp",EDGE,"E7.MirrorCS"),sQuery(id+"F2.wireOp",EDGE,"E8.MirrorCS")])],"isStart":false});
            var Q4;
            Q4=makeQuery(id+"F30.opExtrude","CAP_EDGE",EDGE,{"disambiguationData":[OSD([sQuery(id+"F2.wireOp",EDGE,"E6.bottom"),sQuery(id+"F2.wireOp",EDGE,"E6.right")])],"isStart":false});
            var Q5;
            Q5=makeQuery(id+"F33.opExtrude","CAP_EDGE",EDGE,{"disambiguationData":[OSD([sQuery(id+"F2.wireOp",EDGE,"E5.top"),sQuery(id+"F2.wireOp",EDGE,"E5.left")])],"isStart":false});
            fillet(context, id + "F34", {"entities" : qUnion([Q0, Q1, Q2, Q3, Q4, Q5]), "radius" : 2 * mm, "tangentPropagation" : true, "allowEdgeOverflow" : false});
        }
        {
            var Q0;
            Q0=makeQuery(id+"F1.opExtrude","CAP_FACE",FACE,{"disambiguationData":[OSD([sQuery(id+"F0.wireOp",EDGE,"E0.bottom"),sQuery(id+"F0.wireOp",EDGE,"E0.top"),sQuery(id+"F0.wireOp",EDGE,"E0.left"),sQuery(id+"F0.wireOp",EDGE,"E0.right"),sQuery(id+"F0.wireOp",EDGE,"E1.filletArc"),sQuery(id+"F0.wireOp",EDGE,"E2.filletArc"),sQuery(id+"F0.wireOp",EDGE,"E3.filletArc"),sQuery(id+"F0.wireOp",EDGE,"E4.filletArc")])],"isStart":true});
            var sketch = newSketch(context, id + "F35", { "sketchPlane" : qUnion([Q0])});
            skPoint(sketch, "E69", {"position": v(23, -23) * mm});
            skPoint(sketch, "E70", {"position": v(23, 23) * mm});
            skPoint(sketch, "E71", {"position": v(-23, 18.5) * mm});
            skPoint(sketch, "E72", {"position": v(-23, -18.5) * mm});
            skSolve(sketch);
        }
        {
            var Q0;
            Q0=sQuery(id+"F35.wireOp",VERTEX,"E72");
            var Q1;
            Q1=sQuery(id+"F35.wireOp",VERTEX,"E71");
            var Q2;
            Q2=sQuery(id+"F35.wireOp",VERTEX,"E69");
            var Q3;
            Q3=sQuery(id+"F35.wireOp",VERTEX,"E70");
            var Q4;
            Q4=makeQuery(id+"F1.opExtrude","SWEPT_BODY",BODY,{"disambiguationData":[OSD([sQuery(id+"F0.wireOp",EDGE,"E0.bottom"),sQuery(id+"F0.wireOp",EDGE,"E0.top"),sQuery(id+"F0.wireOp",EDGE,"E0.left"),sQuery(id+"F0.wireOp",EDGE,"E0.right"),sQuery(id+"F0.wireOp",EDGE,"E1.filletArc"),sQuery(id+"F0.wireOp",EDGE,"E2.filletArc"),sQuery(id+"F0.wireOp",EDGE,"E3.filletArc"),sQuery(id+"F0.wireOp",EDGE,"E4.filletArc")])]});
            hole(context, id + "F36", {"style" : HoleStyle.SIMPLE, "endStyle" : HoleEndStyle.BLIND, "holeDiameter" : 1.8 * mm, "majorDiameter" : 5 * mm, "holeDepth" : 5 * mm, "isTappedThrough" : true, "tappedDepth" : 6 * mm, "tapClearance" : 3, "locations" : qUnion([Q0, Q1, Q2, Q3]), "scope" : qUnion([Q4])});
        }
    });
